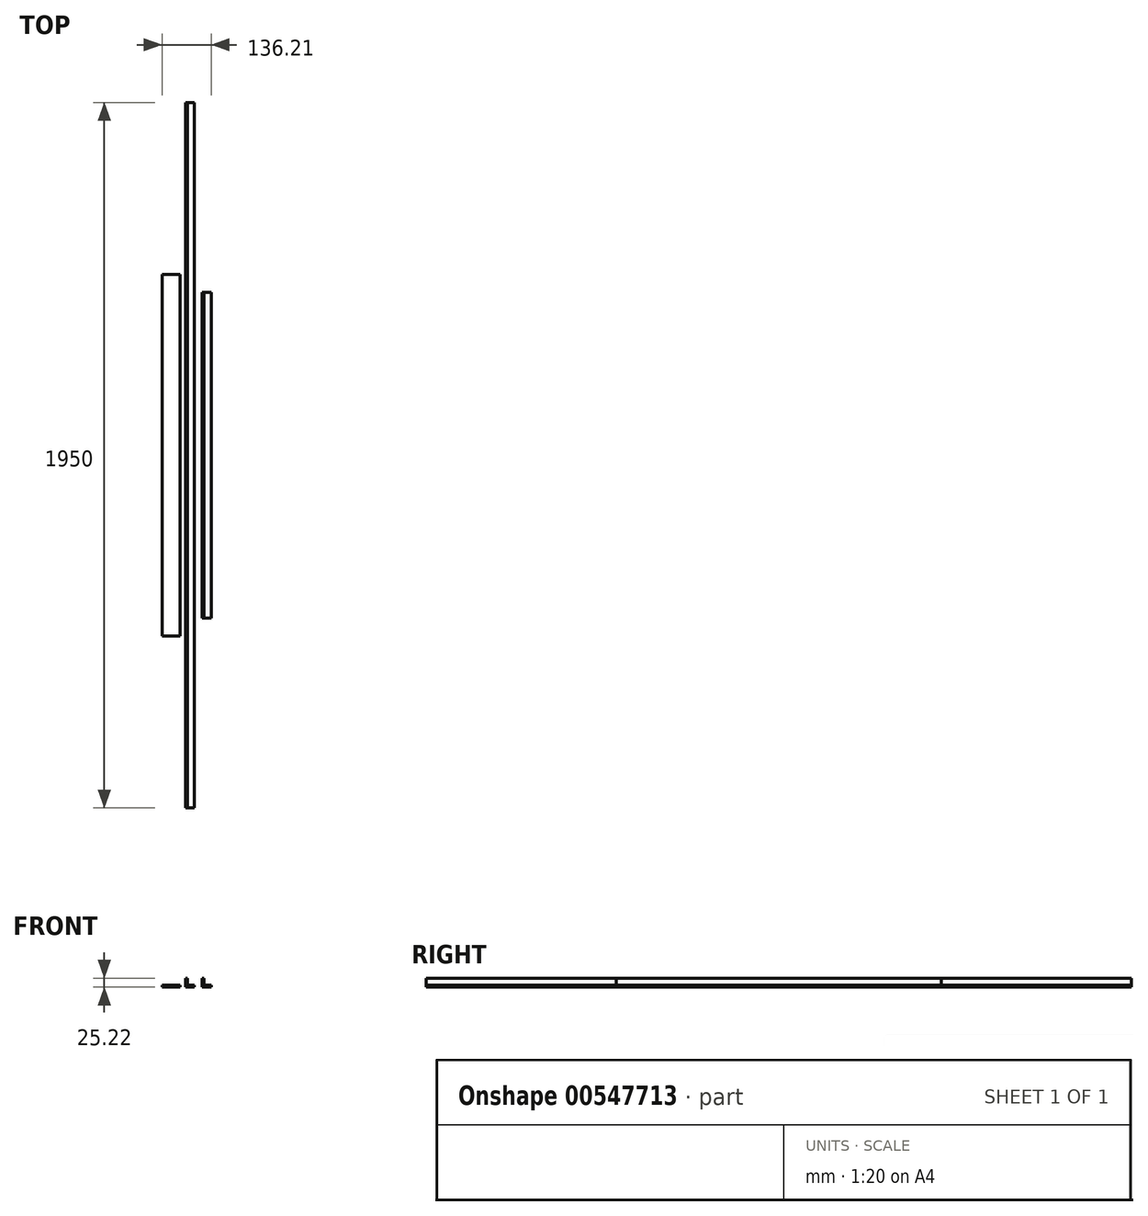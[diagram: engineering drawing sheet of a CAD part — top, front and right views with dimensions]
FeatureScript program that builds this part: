
annotation { "Feature Type Name" : "Feature", "Feature Type Description" : "" }
export const myFeature = defineFeature(function(context is Context, id is Id, definition is map)
    precondition{}
    {
        {
            var Q0;
            Q0=qCreatedBy(makeId("Front.planeOp"),FACE);
            var sketch = newSketch(context, id + "F0", { "sketchPlane" : qUnion([Q0])});
            skLineSegment(sketch, "E0", {"start": v(0, 0) * mm, "end": v(0, 25) * mm});
            skLineSegment(sketch, "E1", {"start": v(0, 25) * mm, "end": v(5, 25) * mm});
            skLineSegment(sketch, "E2", {"start": v(5, 25) * mm, "end": v(5, 5) * mm});
            skLineSegment(sketch, "E3", {"start": v(5, 5) * mm, "end": v(25, 5) * mm});
            skLineSegment(sketch, "E4", {"start": v(25, 5) * mm, "end": v(25, 0) * mm});
            skLineSegment(sketch, "E5", {"start": v(25, 0) * mm, "end": v(0, 0) * mm});
            skSolve(sketch);
        }
        {
            var Q0;
            Q0=qSketchRegion(id+"F0",true);
            extrude(context, id + "F1", {"entities" : qUnion([Q0]), "endBound" : BoundingType.SYMMETRIC, "depth" : 1950 * mm, "offsetDistance" : 25 * mm});
        }
        {
            var Q0;
            Q0=qCreatedBy(makeId("Front.planeOp"),FACE);
            var sketch = newSketch(context, id + "F2", { "sketchPlane" : qUnion([Q0])});
            skLineSegment(sketch, "E6", {"start": v(46.53, 0.22) * mm, "end": v(46.53, 25.22) * mm});
            skLineSegment(sketch, "E7", {"start": v(46.53, 25.22) * mm, "end": v(51.53, 25.22) * mm});
            skLineSegment(sketch, "E8", {"start": v(51.53, 25.22) * mm, "end": v(51.53, 5.22) * mm});
            skLineSegment(sketch, "E9", {"start": v(51.53, 5.22) * mm, "end": v(71.53, 5.22) * mm});
            skLineSegment(sketch, "E10", {"start": v(71.53, 5.22) * mm, "end": v(71.53, 0.22) * mm});
            skLineSegment(sketch, "E11", {"start": v(71.53, 0.22) * mm, "end": v(46.53, 0.22) * mm});
            skSolve(sketch);
        }
        {
            var Q0;
            Q0=qSketchRegion(id+"F2",true);
            extrude(context, id + "F3", {"entities" : qUnion([Q0]), "endBound" : BoundingType.SYMMETRIC, "depth" : 900 * mm, "offsetDistance" : 25 * mm});
        }
        {
            var Q0;
            Q0=qCreatedBy(makeId("Front.planeOp"),FACE);
            var sketch = newSketch(context, id + "F4", { "sketchPlane" : qUnion([Q0])});
            skLineSegment(sketch, "E12.bottom", {"start": v(-14.68, 0) * mm, "end": v(-64.68, 0) * mm});
            skLineSegment(sketch, "E12.top", {"start": v(-14.68, 5) * mm, "end": v(-64.68, 5) * mm});
            skLineSegment(sketch, "E12.left", {"start": v(-14.68, 0) * mm, "end": v(-14.68, 5) * mm});
            skLineSegment(sketch, "E12.right", {"start": v(-64.68, 0) * mm, "end": v(-64.68, 5) * mm});
            skSolve(sketch);
        }
        {
            var Q0;
            Q0 = qSketchRegion(id + "F4", true);
            extrude(context, id + "F5", {"entities" : qUnion([Q0]), "endBound" : BoundingType.SYMMETRIC, "depth" : 1000 * mm, "offsetDistance" : 25 * mm});
        }
    });
